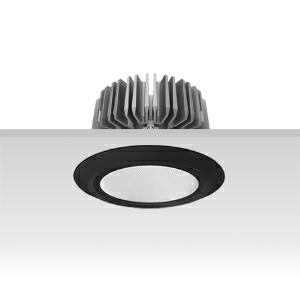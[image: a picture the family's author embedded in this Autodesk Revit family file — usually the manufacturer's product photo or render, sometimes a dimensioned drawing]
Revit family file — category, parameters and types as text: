
# Revit family: 3f_filippi_-_3f_reno_bianco_ampio_3f_filippi_-_30362_a01036_-_3f_reno_150_wh_2000-930_ep_wide___vs_bk_b509
name_source: partatom
category: Lighting Fixtures
units: mm (PartAtom-declared; Revit-internal decimal feet)

## family parameters
Cut with Voids When Loaded = No
Host = Face
Light Source = No
Part Type = Normal
Room Calculation Point = No
Round Connector Dimension = Use Diameter
Shared = No

## types (1)
- 3F Filippi - 3F Reno Bianco Ampio (1 x LED, 1636 lm, 25 W, 3000 K)
    Apparent Load = 25 VA
    Approval mark = ENEC
    CIE Flux Codes = 74 93 99 100 100
    Color Rendering = 90
    Color Temperature = 3000 K
    Control Gear = Electronic ballast
    Default Elevation = 1800 mm
    Description = ILLUMINOTECHNICAL
Luminous efficiency 100% (DLOR 100%, ULOR 0%).
Initial luminous flux of the luminaire 1636 lm.
Emergency luminaire luminous flux BLF 16.7%.
Direct symmetric wide distribution.
Installation Interdistance Transv.D = 1.12 x hu - Long.D = 1.11 x hu.
Tabular UGR (CIE 117 - 4H-8H; S=0.25H; 70/50/20): RUG 22.7 - 22.5.
Beam angle: 74° - 73°.
Luminous efficacy 65 lm/W.
Lifetime (L90/B10): 30000 h. (tq+25°C)
Lifetime (L85/B10): 50000 h. (tq+25°C)
Lifetime (L70/B10): 80000 h. (tq+25°C)
Sudden decreased luminous flux after 50000 hours: 0% (C0).
Photobiological safety in compliance with IEC/TR 62778: RG0 risk exempt, (IEC 62471).
In compliance with IEC/EN 62722-2-1 - IEC/EN 62717 standards.

SOURCE
Compact LED module 2000/930.
Energy efficiency class (UE 2019/2020 - UE 2019/2015): E.
CIE 13.3 Colour rendering index: CRI >90 (R9 >50%).
IES TM-30 Fidelity Index: Rf = 92 Rg = 101.
CCT nominal colour temperature 3000 K.
Colour initial tolerance (MacAdam): SDCM 3.
Zhaga Book 3 compliant.

MECHANICAL
Passive heat dissipator in die-casting aluminium, oversized, for optimum thermal management of the LED module.
Parabolic element with graduated/concentric rings in white polycarbonate.
Transparent external lens with glossy and satin differentiated surfaces, with a cooling and anti-insect system in methacrylate (PMMA).
Fastening spring clips in stainless steel.
Dimensions: diameter 176 mm, height 111 mm. Weight 1.35 kg.
IP44 protection degree for exposed part, IP20 for recessed part.
Mechanical strength to impacts IK06 (1 joule).
Glow-wire test resistance 650°C.

ELECTRICAL
Wiring on a separate unit.
Halogen Free electronic wiring 230V-50/60Hz, power factor 0.90, THD <25%, constant output current, SELV, class II, 1 driver.
Power of the luminaire 25 W.
CE - IEC 60598-1 - EN 60598-1.
EP maintained emergency wiring on board, 1h duration, 24h recharge; compliant with EN 60598-2-22, excluding high risk areas.
SAFE FLICKER: PstLM=<1 and SVM=<0.4 (IEC TR 61547-1 and IEC TR 63158), to ensure a more comfortable and safe light.
Ambient temperature from +5°C to +25°C.
Temperature class T6 max 85°C.
Relative humidity UR: <85%.

INSTALLATION
Pull-up recessed fitting.
False ceiling carving: 150 mm.
All accessories dedicated to this product are available on the Catalog and on our website www.3F-Filippi.com.

ACCESSORIES
A01036 - Anti-glare microprismatic VS moulded glass, tempered, not flammable, locked and in line with the trim, in black polycarbonate.

APPLICATIONS
Environments: architectural, commercial, exhibition areas, transit areas, corridors, shops, display windows, service areas.
In false ceilings with narrow voids.

WARNING
Luminaire designed for disposal/recycling at end-of-life.
Replaceable (LED only) light source by a professional. Replaceable control gear by a professional.
    Height = 0 mm  [stored 0 ft]
    Lamp = 1 x LED
    Lamp Light Flux = 1636 lm
    Lamp Power = 25 W
    Lamp count = 1
    Length = 176 mm
    Lifetime = 50000 h
    Luminous efficacy = 65 lm/W
    Manufacturer = 3F Filippi
    ModVariant = No
    Model = 3F Filippi - 30362+A01036 - 3F Reno 150 WH 2000-930 EP WIDE + VS BK
    Mounting Place = Ceiling
    Mounting Type = Recessed
    Number of Poles = 1
    OnlyDefault = Yes
    Power Factor = 1
    Product Name = 3F Filippi - 3F Reno Bianco Ampio
    Product group = recessed luminaire
    ProductGroupID = 4
    Protection Class = Protection class II
    Protection Degree = IP 20
    RLX_Detail_Level = 1
    RLX_Emergency_Light_Flux = 0 lm
    RLX_Emergency_Type = 0
    RLX_Emergency_Type_DB = No
    RlxData = <blob elided: 85181 chars, md5=aa30afbe>
    Socket = socket
    Standby Power = 0 W
    System Light Flux = 1636 lm
    System Power = 25 W
    Type Comments = Product without accessories
    Type Image = 3ffilippi_3f_reno_150_bk_vs_smp.jpg
    URL = http://relux.com
    VarID = ---
    Voltage = 0 V
    Weight = 0.00 kg
    Width = 0 mm  [stored 0 ft]

note: [stored X ft] marks values corroborated as IEEE doubles in the binary element streams (Revit-internal decimal feet)

## geometry (parser evidence)
native form markers: Blend x4, Sweep x12
no freeform markers — native parametric forms only
